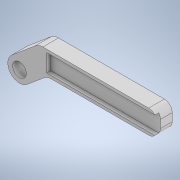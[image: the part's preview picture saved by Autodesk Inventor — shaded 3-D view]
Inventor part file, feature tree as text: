
AUTODESK INVENTOR PART (.ipt)
format: ipt  version: 2020 (Build 240168000, 168)  size: 131,072 bytes
history: native  units: mm
features: extrude x2, sketch x2
ambient origin geometry x8: Origin, YZ Plane, XZ Plane, XY Plane, X Axis, Y Axis, Z Axis, Center Point
bodies: Solid1 (feature_tree)
feature tree (4):
  extrude  "Extrusion1"  Depth=6.0mm
  extrude  "Extrusion2"  Depth=1.0mm
  sketch  "Sketch1"  dims[d0=6.0mm d1=6.0mm]
  sketch  "Sketch2"  dims[d2=3.0mm d3=24.43461mm d4=2.0mm d5=2.0mm d6=35.0mm d7=3.5mm d8=4.0mm d9=0.0mm d10=4.5mm d11=28.0mm d12=1.0mm d13=0.0mm]
